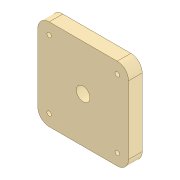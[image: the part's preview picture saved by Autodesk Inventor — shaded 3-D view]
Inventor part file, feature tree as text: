
AUTODESK INVENTOR PART (.ipt)
format: ipt  version: 2020 (Build 240168000, 168)  size: 110,592 bytes
history: native  units: mm
features: other x5, extrude x1
ambient origin geometry x8: Origin, YZ Plane, XZ Plane, XY Plane, X Axis, Y Axis, Z Axis, Center Point
bodies: Body1 (feature_tree)
feature tree (6):
  other  "Sólido1"
  other  "Plano de trabalho1"
  extrude  "Extrusão1"  Depth=12.0mm
  other  "<userpath>\OneDrive\Área de Trabalho\Calorimetro 2022\Inventor\parte_superior.iam"
  other  "parte_superior.iam"
  other  "Corpo_1:4"
